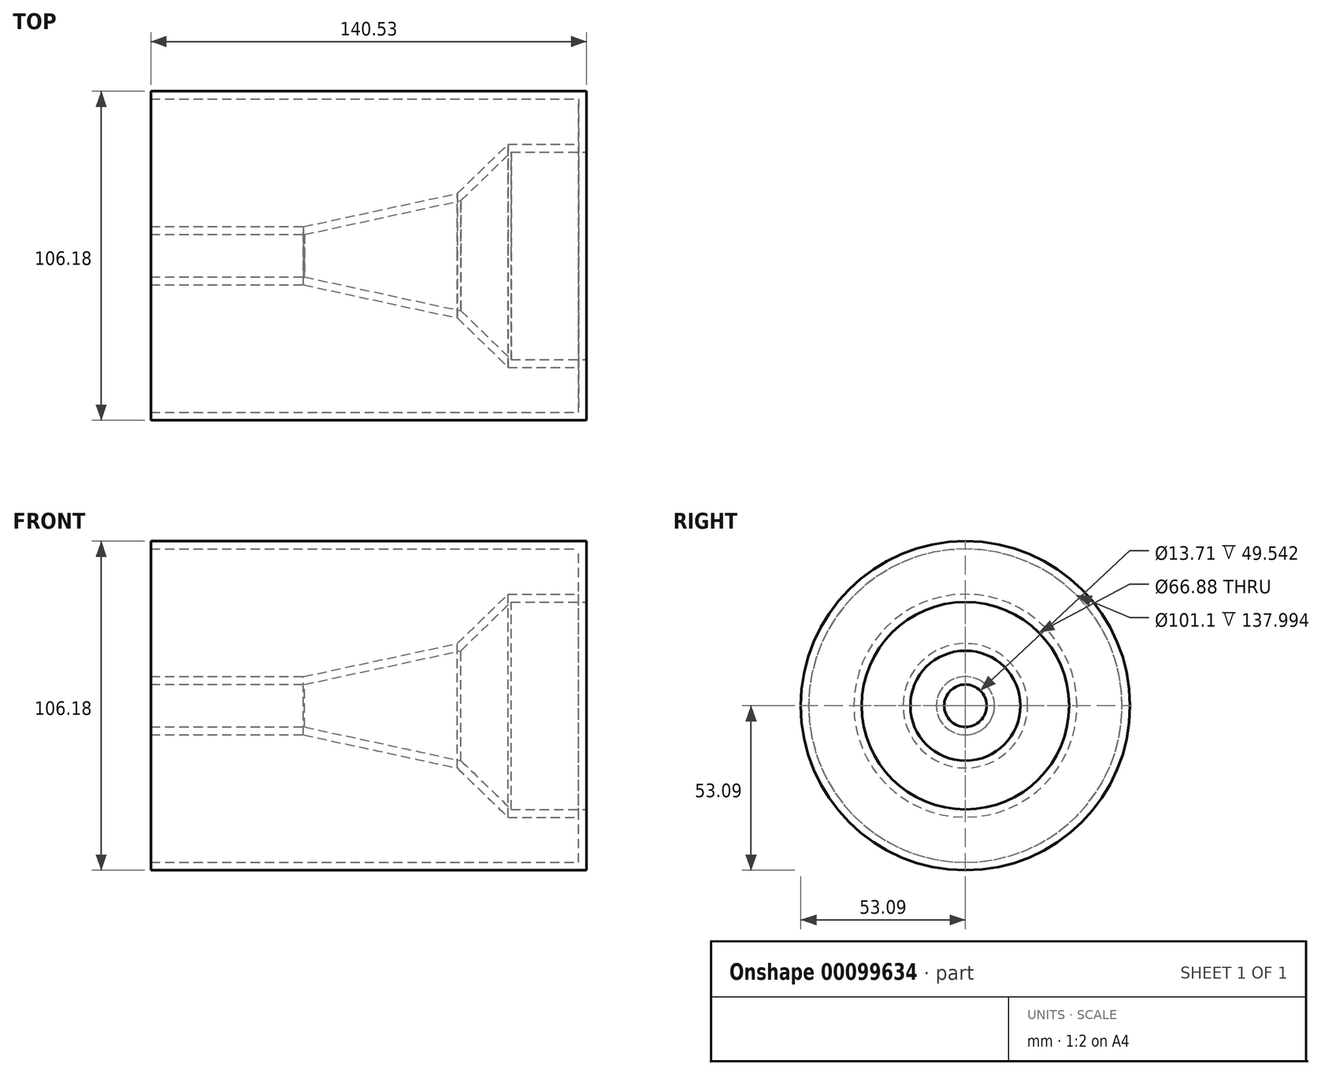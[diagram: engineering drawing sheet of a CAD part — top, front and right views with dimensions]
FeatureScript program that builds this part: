
annotation { "Feature Type Name" : "Feature", "Feature Type Description" : "" }
export const myFeature = defineFeature(function(context is Context, id is Id, definition is map)
    precondition{}
    {
        {
            var Q0;
            Q0=qCreatedBy(makeId("Top.planeOp"),FACE);
            var sketch = newSketch(context, id + "F0", { "sketchPlane" : qUnion([Q0])});
            skLineSegment(sketch, "E0", {"start": v(-70.35, 6.85) * mm, "end": v(-20.8, 6.85) * mm});
            skLineSegment(sketch, "E1", {"start": v(-20.8, 6.85) * mm, "end": v(29.73, 17.75) * mm});
            skLineSegment(sketch, "E2", {"start": v(29.73, 17.75) * mm, "end": v(45.9, 33.44) * mm});
            skLineSegment(sketch, "E3", {"start": v(45.9, 33.44) * mm, "end": v(70.18, 33.44) * mm});
            skLineSegment(sketch, "E4", {"start": v(70.18, 33.44) * mm, "end": v(70.18, 53.1) * mm});
            skLineSegment(sketch, "E5", {"start": v(70.18, 53.1) * mm, "end": v(-70.35, 53.1) * mm});
            skLineSegment(sketch, "E6", {"start": v(-70.35, 53.1) * mm, "end": v(-70.35, 6.85) * mm});
            skLineSegment(sketch, "E7", {"start": v(0, 0) * mm, "end": v(-84.12, 0) * mm});
            skSolve(sketch);
        }
        {
            var Q0;
            Q0=makeQuery(id+"F0.imprint","IMPRINT",FACE,{"disambiguationData":[TD([[makeQuery(id+"F0.imprint","IMPRINT",EDGE,{"derivedFrom":sQuery(id+"F0.wireOp",EDGE,"E0")}),1.0]])]});
            var Q1;
            Q1=sQuery(id+"F0.wireOp",EDGE,"E7");
            revolve(context, id + "F1", {"entities" : qUnion([Q0]), "axis" : qUnion([Q1]), "revolveType" : RevolveType.FULL});
        }
        {
            var Q0;
            Q0=makeQuery(id+"F1.opRevolve","SWEPT_FACE",FACE,{"disambiguationData":[OSD([sQuery(id+"F0.wireOp",EDGE,"E6")])]});
            shell(context, id + "F2", {"entities" : qUnion([Q0]), "thickness" : 2.54 * mm});
        }
    });
